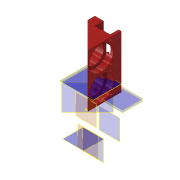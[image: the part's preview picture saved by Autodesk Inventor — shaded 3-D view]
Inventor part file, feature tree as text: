
AUTODESK INVENTOR PART (.ipt)
format: ipt  version: 2022 (Build 260153000, 153)  size: 378,880 bytes
history: native  units: mm
features: plane x13, extrude x12, other x12, sketch x11, projected_geometry x7, reference x6, pattern_linear x1
ambient origin geometry x8: Origin, YZ Plane, XZ Plane, XY Plane, X Axis, Y Axis, Z Axis, Center Point
bodies: Solid1 (feature_tree)
feature tree (62):
  plane  "Work Plane1"
  plane  "Work Plane4"
  extrude  "Extrusion1"  Depth=5.0mm
  plane  "Work Plane5"
  plane  "Work Plane6"
  extrude  "Extrusion4"  Depth=7.0mm TaperAngle=0.0deg
  extrude  "Extrusion9"  Depth=3.3mm TaperAngle=0.0deg
  extrude  "Extrusion3"  Depth=10.0mm
  extrude  "Extrusion13"  Depth=10.0mm TaperAngle=0.0deg
  plane  "Arbeitsebene13"
  plane  "Arbeitsebene16"
  plane  "Work Plane11"
  plane  "Arbeitsebene12"
  plane  "Arbeitsebene15"
  extrude  "Extrusion17"  TaperAngle=135.0deg  [1 undecoded]
  plane  "Arbeitsebene14"
  plane  "Arbeitsebene17"
  extrude  "Extrusion21"  Depth=26.0mm
  pattern_linear  "Rechteckige Anordnung5"  Spacing1=5.0mm  [1 undecoded]
  extrude  "Extrusion22"  Depth=10.0mm
  extrude  "Extrusion23"  Depth=10.0mm
  extrude  "Extrusion24"  Depth=10.0mm
  extrude  "Extrusion25"  Depth=10.0mm
  extrude  "Extrusion26"  Depth=10.0mm TaperAngle=0.0deg
  other  "Work Point1"
  plane  "Work Plane2"
  plane  "Work Plane3"
  sketch  "Sketch1"  dims[d0=2.0mm d1=5.0mm]
  reference  "Reference2"
  reference  "Reference4"
  sketch  "Sketch3"  dims[d4=28.0mm d5=0.0mm d11=7.0mm d12=0.0mm]
  sketch  "Sketch4"  dims[d14=5.6mm d15=0.0mm d39=3.3mm d40=0.0mm]
  reference  "Reference7"
  sketch  "Sketch9"  dims[d58=10.0mm d59=0.0mm d90=20.0mm]
  sketch  "Sketch13"  dims[d93=2.9mm d94=10.0mm d95=0.0mm]
  sketch  "Skizze20"  dims[d96=27.5mm d97=135.0deg]
  projected_geometry  "Projizierte Kontur14"
  projected_geometry  "Projizierte Kontur15"
  projected_geometry  "Projizierte Kontur16"
  sketch  "Skizze25"  dims[d98=13.75mm d100=26.0mm]
  projected_geometry  "Projizierte Kontur17"
  sketch  "Skizze27"  dims[d108=0.2mm]
  reference  "Referenz29"
  reference  "Referenz30"
  projected_geometry  "Projizierte Kontur18"
  sketch  "Skizze28"  dims[d142=2.8mm]
  reference  "Referenz31"
  projected_geometry  "Projizierte Kontur19"
  sketch  "Skizze29"  dims[d143=2.8mm]
  sketch  "Skizze30"  dims[d144=2.5mm d146=5.0mm d147=2.5mm d148=5.0mm d149=16.0mm d150=3.0mm d151=10.0mm d152=0.0mm d153=20.0mm d155=28.0mm d157=10.0mm d158=-0.349066mm d159=7.5mm d160=30.0mm d161=0.0mm d163=0.6mm d164=3.5mm d165=3.5mm d166=30.0mm d167=0.0mm d168=7.0mm d169=0.0mm d170=2.8mm d171=2.8mm d172=6.0mm d173=0.0mm d174=2.8mm d175=2.8mm d176=2.8mm d177=2.8mm d178=2.8mm d179=2.8mm d180=11.0mm d181=11.0mm d182=10.0mm d183=10.0mm]
  projected_geometry  "Projizierte Kontur20"
  other  "30_Cube_Insert_Filter_Revolver_Filters_v3.iam"
  other  "00_Comar_Filter_25Dia:2"
  other  "Assembly_Cube_Dichroic_Beamsplitter_multi_motorized_revolver_25x35_v3.iam"
  other  "10_Cube_1x1_IM:2"
  other  "10_Cube_1x1_IM:3"
  other  "Assembly_Cube_Dichroic_Beamsplitter_multi_motorized_25x35_linearmotor_v3.iam"
  other  "Assebmly_Linear_Stepper_90mm:2"
  other  "00_Linear_Stepper_90mm_slide:1"
  other  "00_Linear_Stepper_90mm:1"
  other  "30_Cube_Insert_Filter_Revolver_Filters_v3:1"
  other  "00_Chroma_Dichroic_25x,3x1:1"
note: 2 required parameter values undecoded (feature->parameter linkage not recoverable at this tier; creation-order binding heuristic only, values carry confidence <= 0.55)
